# Revit family: Flushometer-Sensor-Sloan-CX_198_Series
name_source: partatom
category: Plumbing Fixtures
revit_build: Autodesk Revit 2014 (Build: 20130308_1515(x64)
units: mm (PartAtom-declared; Revit-internal decimal feet)

## types (3) — shared parameters
ADA Compliant = Yes
CW Connection = Yes
CWFU = 10
Cold Water Connection Diameter = 1 1/2"
Connection Diameter = 1 1/2"
Connection Inlet Description = 1-1/2” NPT (female) Inlet standard
Connection Outlet Description = 1-1/2” NPSM Outlet standard
Default Elevation = 0"
Faceplate Material = Rough Brass-Sloan-Polished Chrome
Finishes = Polished Chrome, PVDSF, PVDPB, PVDBN, PVDMB
Fixture Type = Closet
HW Connection = No
Height = 9 13/32"
Manufacturer = Sloan
Material = Rough Brass-Sloan-Polished Chrome
Model = CX 198
Operating Pressure = 10-100 psi (0.7-7 bars)
Price = Prices may vary. Please consult Manufacturer Representative for most up-to-date price list.
URL = http://www.sloan.com
Vent Connection = No
WFU = 10
Waste Connection = No
Width = 9"
zero-valued in all types: HWFU

## per-type parameters (varying)
| type | Flush Cycle |
| CX 198-0.5 | 0.5 gpf/1.9 Lpf |
| CX 198-0.25 | 0.25 gpf/0.9 Lpf |
| CX 198-0.125 | 0.125 gpf/0.5 Lpf |

## geometry (parser evidence)
native form markers: Sweep x1
no freeform markers — native parametric forms only
